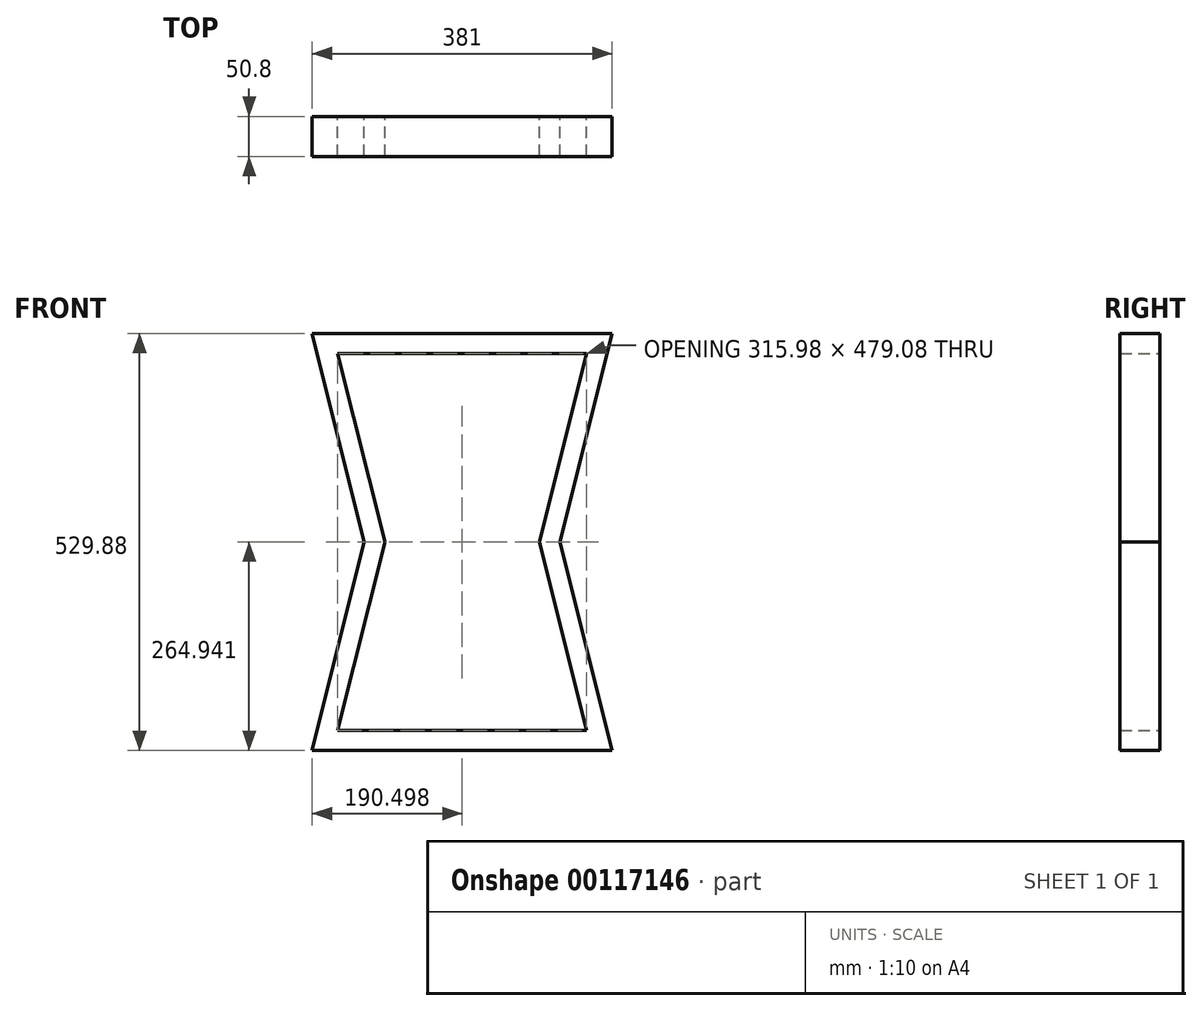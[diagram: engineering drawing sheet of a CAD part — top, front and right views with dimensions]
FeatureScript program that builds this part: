
annotation { "Feature Type Name" : "Feature", "Feature Type Description" : "" }
export const myFeature = defineFeature(function(context is Context, id is Id, definition is map)
    precondition{}
    {
        {
            var Q0;
            Q0=qCreatedBy(makeId("Front.planeOp"),FACE);
            var sketch = newSketch(context, id + "F0", { "sketchPlane" : qUnion([Q0])});
            skLineSegment(sketch, "E0.bottom", {"start": v(-213.5, 251.62) * mm, "end": v(167.5, 251.62) * mm});
            skLineSegment(sketch, "E0.top", {"start": v(-213.5, -278.26) * mm, "end": v(167.5, -278.26) * mm});
            skLineSegment(sketch, "E1", {"start": v(-213.5, 251.62) * mm, "end": v(-147.45, -13.32) * mm});
            skLineSegment(sketch, "E2", {"start": v(-147.45, -13.32) * mm, "end": v(-213.5, -278.26) * mm});
            skLineSegment(sketch, "E3", {"start": v(167.5, 251.62) * mm, "end": v(101.44, -13.32) * mm});
            skLineSegment(sketch, "E4", {"start": v(101.44, -13.32) * mm, "end": v(167.5, -278.26) * mm});
            skLineSegment(sketch, "E5.0", {"start": v(-181, 226.22) * mm, "end": v(-121.27, -13.32) * mm});
            skLineSegment(sketch, "E5.1", {"start": v(134.99, 226.22) * mm, "end": v(75.26, -13.32) * mm});
            skLineSegment(sketch, "E5.2", {"start": v(75.26, -13.32) * mm, "end": v(134.99, -252.86) * mm});
            skLineSegment(sketch, "E5.3", {"start": v(-181, 226.22) * mm, "end": v(134.99, 226.22) * mm});
            skLineSegment(sketch, "E5.4", {"start": v(-181, -252.86) * mm, "end": v(134.99, -252.86) * mm});
            skLineSegment(sketch, "E5.5", {"start": v(-121.27, -13.32) * mm, "end": v(-181, -252.86) * mm});
            skLineSegment(sketch, "E6", {"start": v(-181, 226.22) * mm, "end": v(-187.32, 251.62) * mm});
            skLineSegment(sketch, "E7", {"start": v(134.99, 226.22) * mm, "end": v(141.32, 251.62) * mm});
            skLineSegment(sketch, "E8", {"start": v(-147.45, -13.32) * mm, "end": v(-121.27, -13.32) * mm});
            skLineSegment(sketch, "E9", {"start": v(75.26, -13.32) * mm, "end": v(101.44, -13.32) * mm});
            skLineSegment(sketch, "E10", {"start": v(-181, -252.86) * mm, "end": v(-187.32, -278.26) * mm});
            skLineSegment(sketch, "E11", {"start": v(134.99, -252.86) * mm, "end": v(141.32, -278.26) * mm});
            skSolve(sketch);
        }
        {
            var Q0;
            Q0=makeQuery(id+"F0.imprint","IMPRINT",FACE,{"disambiguationData":[TD([[makeQuery(id+"F0.imprint","IMPRINT",EDGE,{"derivedFrom":sQuery(id+"F0.wireOp",EDGE,"E0.bottom")}),-1.0]])]});
            var Q1;
            {var subQ1=sQuery(id+"F0.wireOp",EDGE,"E1");Q1=makeQuery(id+"F0.imprint","IMPRINT",FACE,{"disambiguationData":[TD([[makeQuery(id+"F0.imprint","IMPRINT",EDGE,{"derivedFrom":subQ1}),1.0]])]});}
            var Q2;
            {var subQ1=sQuery(id+"F0.wireOp",EDGE,"E3");Q2=makeQuery(id+"F0.imprint","IMPRINT",FACE,{"disambiguationData":[TD([[makeQuery(id+"F0.imprint","IMPRINT",EDGE,{"derivedFrom":subQ1}),-1.0]])]});}
            var Q3;
            Q3=makeQuery(id+"F0.imprint","IMPRINT",FACE,{"disambiguationData":[TD([[makeQuery(id+"F0.imprint","IMPRINT",EDGE,{"derivedFrom":sQuery(id+"F0.wireOp",EDGE,"E0.top")}),1.0]])]});
            var Q4;
            {var subQ0=sQuery(id+"F0.wireOp",EDGE,"E2");Q4=makeQuery(id+"F0.imprint","IMPRINT",FACE,{"disambiguationData":[TD([[makeQuery(id+"F0.imprint","IMPRINT",EDGE,{"derivedFrom":subQ0}),1.0]])]});}
            var Q5;
            {var subQ0=sQuery(id+"F0.wireOp",EDGE,"E4");Q5=makeQuery(id+"F0.imprint","IMPRINT",FACE,{"disambiguationData":[TD([[makeQuery(id+"F0.imprint","IMPRINT",EDGE,{"derivedFrom":subQ0}),-1.0]])]});}
            extrude(context, id + "F1", {"entities" : qUnion([Q0, Q1, Q2, Q3, Q4, Q5]), "depth" : 50.8 * mm});
        }
    });
